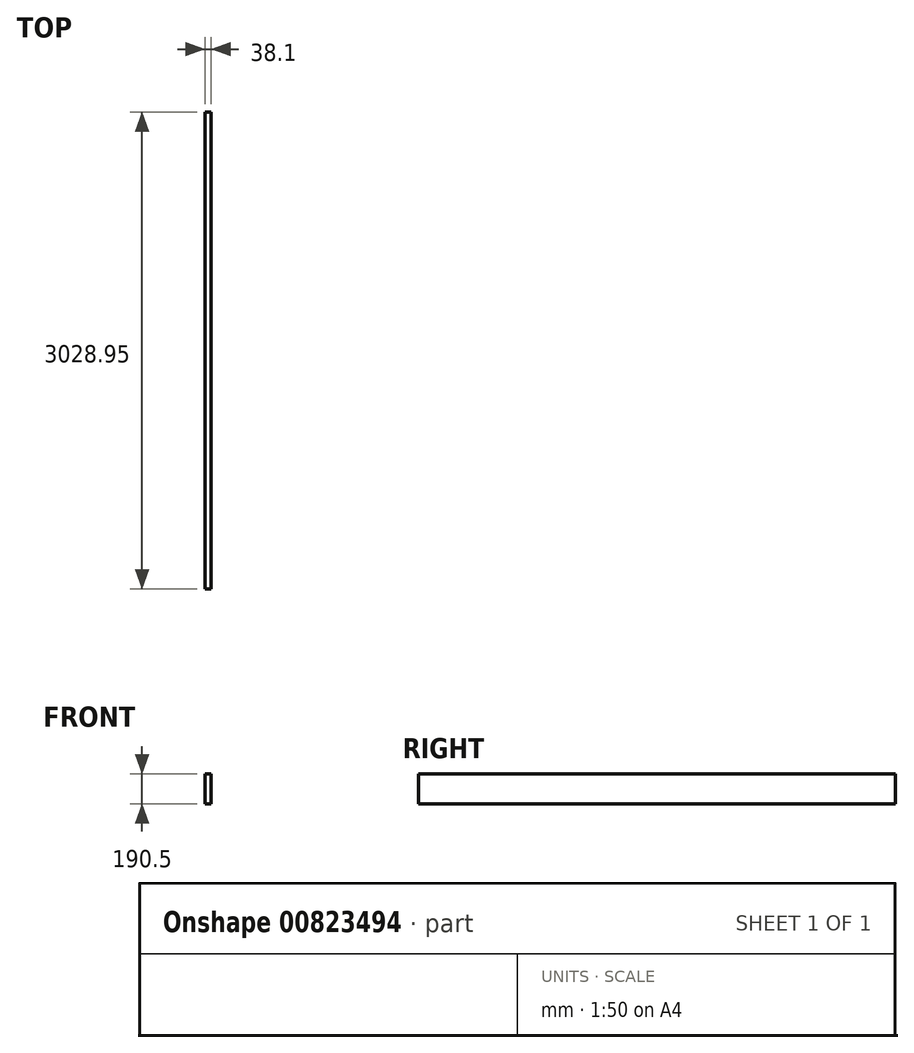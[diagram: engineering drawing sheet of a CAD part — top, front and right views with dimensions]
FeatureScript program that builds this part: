
annotation { "Feature Type Name" : "Feature", "Feature Type Description" : "" }
export const myFeature = defineFeature(function(context is Context, id is Id, definition is map)
    precondition{}
    {
        {
            var Q0;
            Q0=qCreatedBy(makeId("Front.planeOp"),FACE);
            var sketch = newSketch(context, id + "F0", { "sketchPlane" : qUnion([Q0])});
            skLineSegment(sketch, "E0.bottom", {"start": v(0, 0) * mm, "end": v(38.1, 0) * mm});
            skLineSegment(sketch, "E0.top", {"start": v(0, 190.5) * mm, "end": v(38.1, 190.5) * mm});
            skLineSegment(sketch, "E0.left", {"start": v(0, 0) * mm, "end": v(0, 190.5) * mm});
            skLineSegment(sketch, "E0.right", {"start": v(38.1, 0) * mm, "end": v(38.1, 190.5) * mm});
            skSolve(sketch);
        }
        {
            var Q0;
            Q0=qSketchRegion(id+"F0",true);
            extrude(context, id + "F1", {"entities" : qUnion([Q0]), "depth" : 3028.95 * mm, "offsetDistance" : 25.4 * mm});
        }
    });
